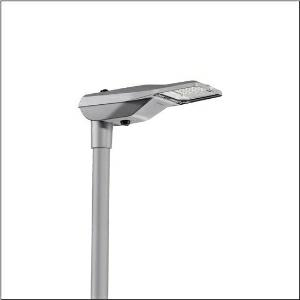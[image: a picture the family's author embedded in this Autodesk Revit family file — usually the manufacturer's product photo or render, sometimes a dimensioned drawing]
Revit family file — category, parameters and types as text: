
# Revit family: streetlight_sl_21_iq_micro___st1_0a_5xe1d21y08cb_9119
name_source: partatom
category: Lighting Fixtures
units: mm (PartAtom-declared; Revit-internal decimal feet)

## family parameters
Cut with Voids When Loaded = No
Host = Face
Light Source = No
Part Type = Normal
Room Calculation Point = No
Round Connector Dimension = Use Diameter
Shared = No

## types (1)
- --- (1 x LED, 2310 lm, 19.1 W, 2200K)
    Apparent Load = 19 VA
    CIE Flux Codes = 37 72 97 100 100
    Color Rendering = 70
    Color Temperature = 2200K
    Default Elevation = 1800 mm
    Description = Streetlight SL 21 iQ micro, mast luminaire, primary light control with lens, of PMMA, primary optical cover: cover, of toughened safety glass, transparent, light distribution: ST1.0a, light emission: direct distribution, primary light characteristic: asymmetric, installation type: post-top, side-entry, LED, High Power LED, rated luminous flux: 2.310lm, luminous efficacy: 121lm/W, light colour: 722, colour temperature: 2200K, control gear: iQ-Street Remote, D4i with power reduction, control: pre-setting: logarithmic dimming characteristic, Street-Remote, Auto-Match, Temp-Guard, Lumen-Switch, Night-Set, Smart-Wire, Light-Fading, Desk-Remote (wireless, voltage-free reading and setting of iQ features in the workshop via application-optimized NFC function/RFID function), optimised constant luminous flux control (CLO 2.0), mains connection: 220..240V, AC, 50/60Hz, start of lifetime: 19W, end of service life: 20W, reduction: 9W, luminaire housing, of diecast aluminium, powder-coated, SITECO metallic grey (DB 702S), corrosivity category C5 high according to DIN EN ISO 12944, please order mast flange separately, inclination adjustable: 0°, 5°, 10°, 15°, sealing non-destructively replaceable, multi-level sealing system, length: 528mm, width: 235mm, height: 110mm, mast flange for spigot size: 42mm (side-entry): 5XC10008XM4, 60/48mm (side-entry/post-top): 5XC10108XM2, 76/60mm (side-entry/post-top): 5XC10108XM1, mounting height: 4..8m, Smart Interface below and above, protection rating (complete): IP66, insulation class (complete): insulation class II (safety insulation), certification: CE, ENEC, ENEC+, VDE, impact resistance: IK10, permissible operating ambient temperature for outdoor applications: -40..+50°C, standard-compliant lighting for roads and squares, packaging unit: 1 piece

Light Distribution: ST1.0a
    Height = 110 mm
    Lamp = 1 x LED
    Lamp Light Flux = 2310 lm
    Lamp Power = 19.1 W
    Lamp count = 1
    Length = 528 mm
    Luminous efficacy = 121 lm/W
    Manufacturer = Siteco
    ModVariant = No
    Model = 5XE1D21Y08CB
    Number of Poles = 1
    OnlyDefault = Yes
    Power Factor = 1
    Product Name = Streetlight SL 21 iQ micro | ST1.0a
    Product group = mast luminaire | pylon top
    ProductGroupID = 6100
    Protection Class = Protection class II
    Protection Degree = IP 66
    RLX_Detail_Level = 1
    RLX_Emergency_Light_Flux = 0 lm
    RLX_Emergency_Type = 0
    RLX_Emergency_Type_DB = No
    RlxData = <blob elided: 99009 chars, md5=ae6dc4d7>
    Socket = socket
    Standby Power = 0 W
    System Light Flux = 2310 lm
    System Power = 19 W
    Type Comments = factory setting: luminous flux: 100 % | dim-lin: 254 | 387 mA
    Type Image = l_1007239.jpg
    URL = http://relux.com
    VarID = @adj_115731
    Voltage = 0 V
    Weight = 0.00 kg
    Width = 235 mm

## geometry (parser evidence)
native form markers: Blend x4, Sweep x10
no freeform markers — native parametric forms only
